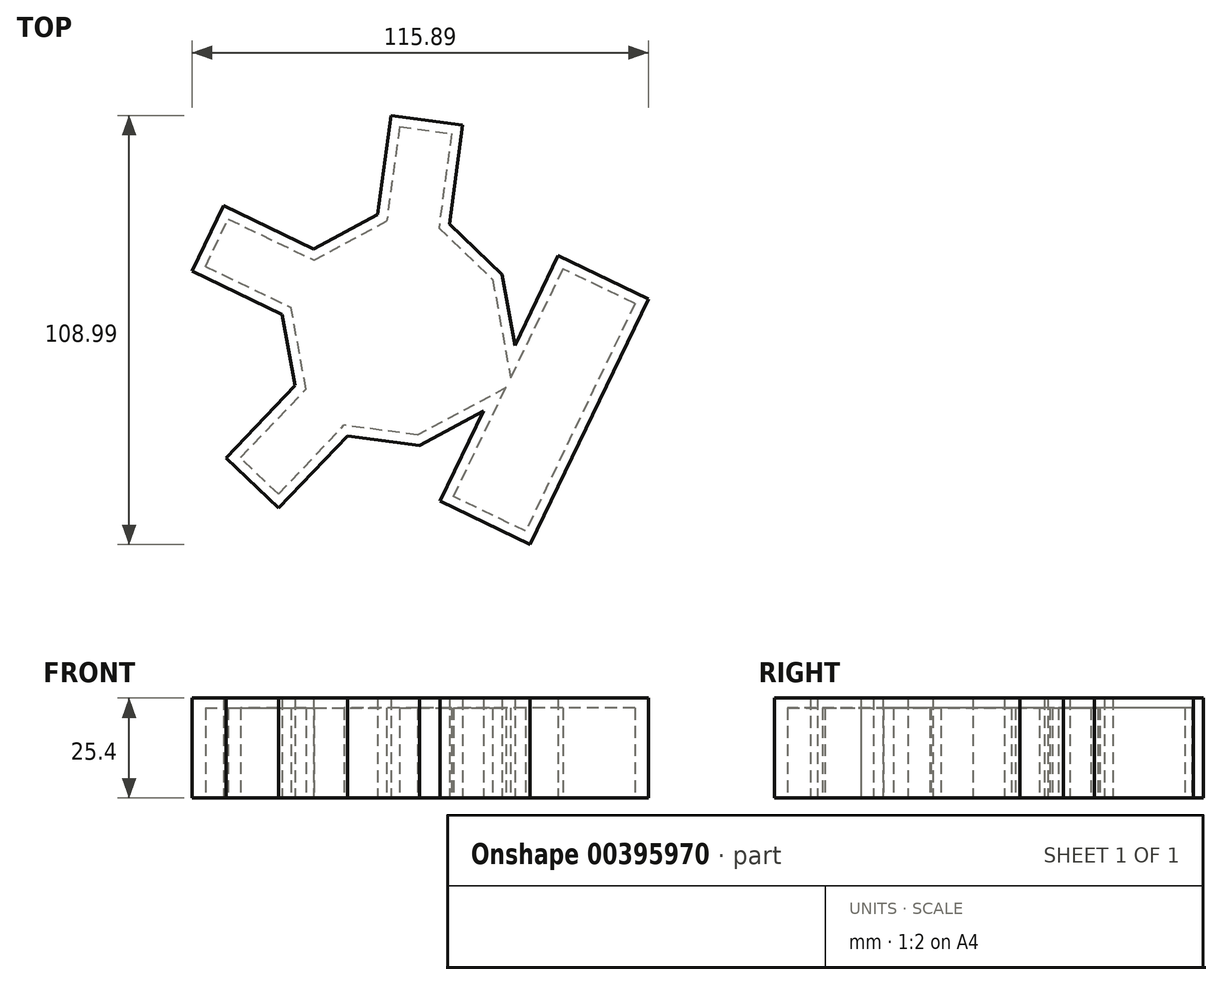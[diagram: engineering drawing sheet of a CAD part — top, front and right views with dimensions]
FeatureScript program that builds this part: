
annotation { "Feature Type Name" : "Feature", "Feature Type Description" : "" }
export const myFeature = defineFeature(function(context is Context, id is Id, definition is map)
    precondition{}
    {
        {
            var Q0;
            Q0=qCreatedBy(makeId("Top.planeOp"),FACE);
            var sketch = newSketch(context, id + "F0", { "sketchPlane" : qUnion([Q0])});
            skCircle(sketch, "E0.cCircle", {"center": v(-48.87, 21.25) * mm, "radius": 28.36 * mm, "construction": true});
            skLineSegment(sketch, "E0.0", {"start": v(-19.32, 17.27) * mm, "end": v(-27.3, 0.66) * mm});
            skLineSegment(sketch, "E0.1", {"start": v(-27.3, 0.66) * mm, "end": v(-43.52, -8.08) * mm});
            skLineSegment(sketch, "E0.2", {"start": v(-43.52, -8.08) * mm, "end": v(-61.79, -5.63) * mm});
            skLineSegment(sketch, "E0.3", {"start": v(-61.79, -5.63) * mm, "end": v(-75.11, 7.1) * mm});
            skLineSegment(sketch, "E0.4", {"start": v(-75.11, 7.1) * mm, "end": v(-78.42, 25.23) * mm});
            skLineSegment(sketch, "E0.5", {"start": v(-78.42, 25.23) * mm, "end": v(-70.44, 41.84) * mm});
            skLineSegment(sketch, "E0.6", {"start": v(-70.44, 41.84) * mm, "end": v(-54.22, 50.58) * mm});
            skLineSegment(sketch, "E0.7", {"start": v(-54.22, 50.58) * mm, "end": v(-35.95, 48.12) * mm});
            skLineSegment(sketch, "E0.8", {"start": v(-35.95, 48.12) * mm, "end": v(-22.62, 35.4) * mm});
            skLineSegment(sketch, "E0.9", {"start": v(-22.62, 35.4) * mm, "end": v(-19.32, 17.27) * mm});
            skPoint(sketch, "E0.0.midPoint", {"position": v(-23.31, 8.96) * mm});
            skSolve(sketch);
        }
        {
            var Q0;
            Q0=makeQuery(id+"F0.imprint","IMPRINT",FACE,{"disambiguationData":[TD([[makeQuery(id+"F0.imprint","IMPRINT",EDGE,{"derivedFrom":sQuery(id+"F0.wireOp",EDGE,"E0.0")}),-1.0]])]});
            extrude(context, id + "F1", {"entities" : qUnion([Q0]), "depth" : 25.4 * mm});
        }
        {
            var Q0;
            Q0=makeQuery(id+"F1.opExtrude","SWEPT_FACE",FACE,{"disambiguationData":[OSD([sQuery(id+"F0.wireOp",EDGE,"E0.0")])]});
            extrude(context, id + "F2", {"entities" : qUnion([Q0]), "operationType" : NewBodyOperationType.ADD, "depth" : 25.4 * mm});
        }
        {
            var Q0;
            Q0=makeQuery(id+"F1.opExtrude","SWEPT_FACE",FACE,{"disambiguationData":[OSD([sQuery(id+"F0.wireOp",EDGE,"E0.5")])]});
            extrude(context, id + "F3", {"entities" : qUnion([Q0]), "operationType" : NewBodyOperationType.ADD, "depth" : 25.4 * mm});
        }
        {
            var Q0;
            Q0=makeQuery(id+"F1.opExtrude","SWEPT_FACE",FACE,{"disambiguationData":[OSD([sQuery(id+"F0.wireOp",EDGE,"E0.3")])]});
            extrude(context, id + "F4", {"entities" : qUnion([Q0]), "operationType" : NewBodyOperationType.ADD, "depth" : 25.4 * mm});
        }
        {
            var Q0;
            Q0=makeQuery(id+"F1.opExtrude","SWEPT_FACE",FACE,{"disambiguationData":[OSD([sQuery(id+"F0.wireOp",EDGE,"E0.7")])]});
            extrude(context, id + "F5", {"entities" : qUnion([Q0]), "operationType" : NewBodyOperationType.ADD, "depth" : 25.4 * mm});
        }
        {
            var Q0;
            Q0=makeQuery(id+"F2.opExtrude","SWEPT_FACE",FACE,{"disambiguationData":[OSD([sQuery(id+"F0.wireOp",EDGE,"E0.0"),sQuery(id+"F0.wireOp",EDGE,"E0.9")])]});
            extrude(context, id + "F6", {"entities" : qUnion([Q0]), "operationType" : NewBodyOperationType.ADD, "depth" : 25.4 * mm});
        }
        {
            var Q0;
            Q0=makeQuery(id+"F2.opExtrude","SWEPT_FACE",FACE,{"disambiguationData":[OSD([sQuery(id+"F0.wireOp",EDGE,"E0.0"),sQuery(id+"F0.wireOp",EDGE,"E0.1")])]});
            extrude(context, id + "F7", {"entities" : qUnion([Q0]), "operationType" : NewBodyOperationType.ADD, "depth" : 25.4 * mm});
        }
        {
            var Q0;
            {var subQ0=sQuery(id+"F0.wireOp",EDGE,"E0.1");var subQ1=sQuery(id+"F0.wireOp",EDGE,"E0.0");var subQ2=sQuery(id+"F0.wireOp",EDGE,"E0.9");var subQ3=sQuery(id+"F0.wireOp",EDGE,"E0.7");var subQ4=sQuery(id+"F0.wireOp",EDGE,"E0.3");var subQ5=sQuery(id+"F0.wireOp",EDGE,"E0.5");Q0=makeQuery(id+"F7.boolean.opBoolean","MERGE",FACE,{"derivedFrom":[makeQuery(id+"F6.boolean.opBoolean","MERGE",FACE,{"derivedFrom":[makeQuery(id+"F5.boolean.opBoolean","MERGE",FACE,{"derivedFrom":[makeQuery(id+"F4.boolean.opBoolean","MERGE",FACE,{"derivedFrom":[makeQuery(id+"F3.boolean.opBoolean","MERGE",FACE,{"derivedFrom":[makeQuery(id+"F2.boolean.opBoolean","MERGE",FACE,{"derivedFrom":[makeQuery(id+"F1.opExtrude","CAP_FACE",FACE,{"disambiguationData":[OSD([subQ1,subQ0,sQuery(id+"F0.wireOp",EDGE,"E0.2"),subQ4,sQuery(id+"F0.wireOp",EDGE,"E0.4"),subQ5,sQuery(id+"F0.wireOp",EDGE,"E0.6"),subQ3,sQuery(id+"F0.wireOp",EDGE,"E0.8"),subQ2])],"isStart":true}),makeQuery(id+"F2.opExtrude","SWEPT_FACE",FACE,{"disambiguationData":[OSD([subQ1]),TDD([makeQuery(id+"F1.opExtrude","CAP_EDGE",EDGE,{"disambiguationData":[OSD([subQ1])],"isStart":true})])]})]}),makeQuery(id+"F3.opExtrude","SWEPT_FACE",FACE,{"disambiguationData":[OSD([subQ5]),TDD([makeQuery(id+"F1.opExtrude","CAP_EDGE",EDGE,{"disambiguationData":[OSD([subQ5])],"isStart":true})])]})]}),makeQuery(id+"F4.opExtrude","SWEPT_FACE",FACE,{"disambiguationData":[OSD([subQ4]),TDD([makeQuery(id+"F1.opExtrude","CAP_EDGE",EDGE,{"disambiguationData":[OSD([subQ4])],"isStart":true})])]})]}),makeQuery(id+"F5.opExtrude","SWEPT_FACE",FACE,{"disambiguationData":[OSD([subQ3]),TDD([makeQuery(id+"F1.opExtrude","CAP_EDGE",EDGE,{"disambiguationData":[OSD([subQ3])],"isStart":true})])]})]}),makeQuery(id+"F6.opExtrude","SWEPT_FACE",FACE,{"disambiguationData":[OSD([subQ1,subQ2]),TDD([makeQuery(id+"F2.opExtrude","SWEPT_EDGE",EDGE,{"disambiguationData":[OSD([subQ1,subQ2]),TDD([makeQuery(id+"F1.opExtrude","CAP_VERTEX",VERTEX,{"disambiguationData":[OSD([subQ1,subQ2])],"isStart":true})])]})])]})]}),makeQuery(id+"F7.opExtrude","SWEPT_FACE",FACE,{"disambiguationData":[OSD([subQ1,subQ0]),TDD([makeQuery(id+"F2.opExtrude","SWEPT_EDGE",EDGE,{"disambiguationData":[OSD([subQ1,subQ0]),TDD([makeQuery(id+"F1.opExtrude","CAP_VERTEX",VERTEX,{"disambiguationData":[OSD([subQ1,subQ0])],"isStart":true})])]})])]})]});}
            shell(context, id + "F8", {"entities" : qUnion([Q0]), "thickness" : 2.54 * mm});
        }
    });
